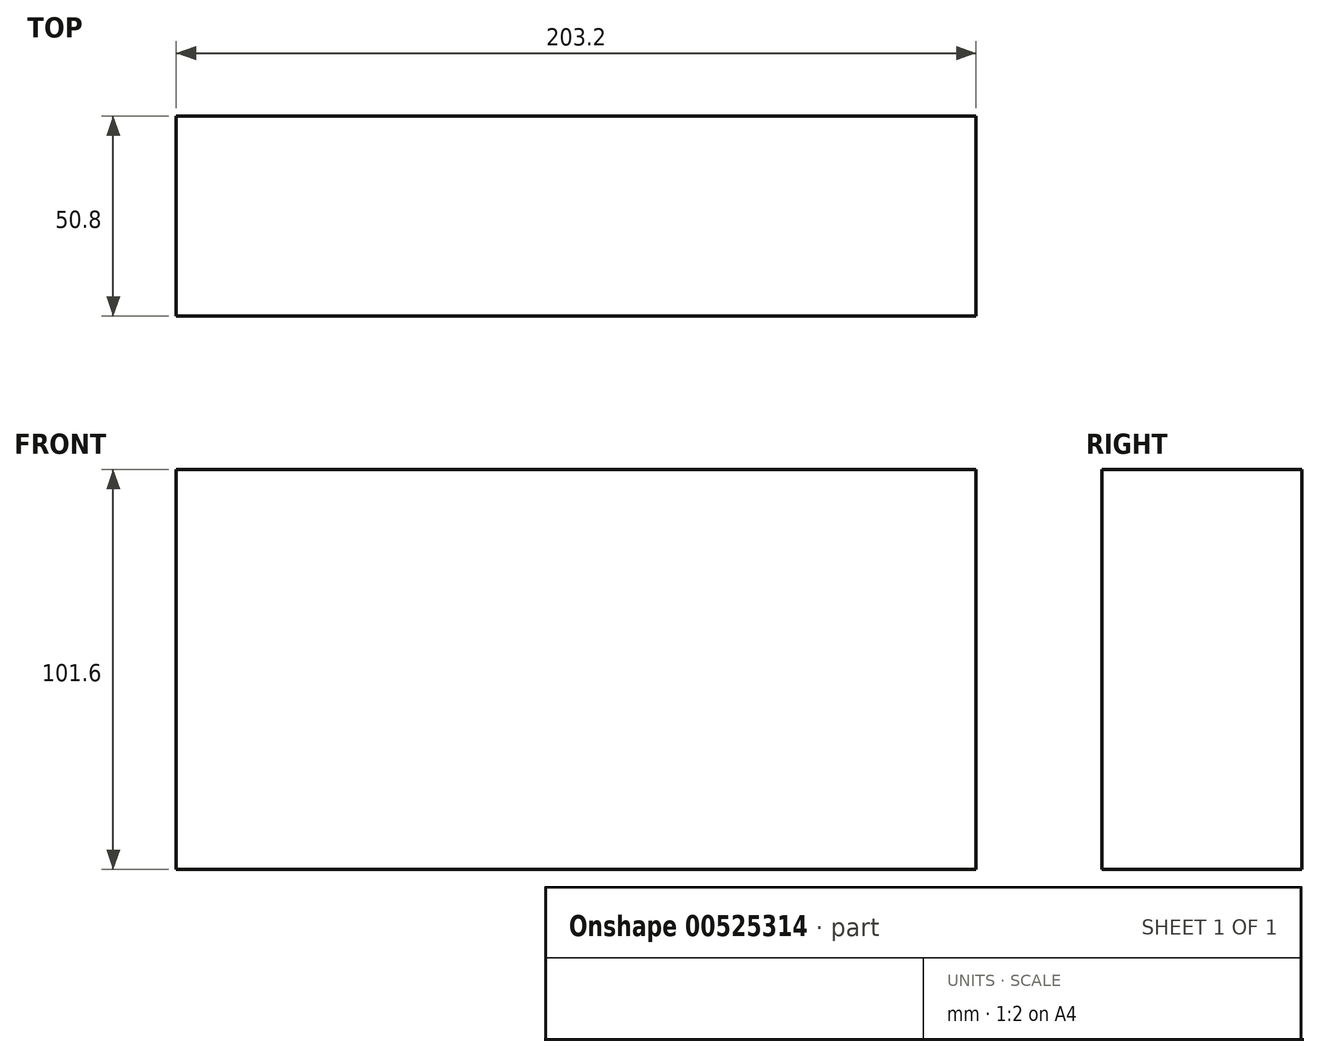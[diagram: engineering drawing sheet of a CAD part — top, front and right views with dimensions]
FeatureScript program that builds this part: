
annotation { "Feature Type Name" : "Feature", "Feature Type Description" : "" }
export const myFeature = defineFeature(function(context is Context, id is Id, definition is map)
    precondition{}
    {
        {
            var Q0;
            Q0=qCreatedBy(makeId("Right.planeOp"),FACE);
            var sketch = newSketch(context, id + "F0", { "sketchPlane" : qUnion([Q0])});
            skLineSegment(sketch, "E0.bottom", {"start": v(0, 0) * mm, "end": v(50.8, 0) * mm});
            skLineSegment(sketch, "E0.top", {"start": v(0, 101.6) * mm, "end": v(50.8, 101.6) * mm});
            skLineSegment(sketch, "E0.left", {"start": v(0, 0) * mm, "end": v(0, 101.6) * mm});
            skLineSegment(sketch, "E0.right", {"start": v(50.8, 0) * mm, "end": v(50.8, 101.6) * mm});
            skSolve(sketch);
        }
        {
            var Q0;
            Q0=makeQuery(id+"F0.imprint","IMPRINT",FACE,{"disambiguationData":[TD([[makeQuery(id+"F0.imprint","IMPRINT",EDGE,{"derivedFrom":sQuery(id+"F0.wireOp",EDGE,"E0.bottom")}),1.0]])]});
            extrude(context, id + "F1", {"entities" : qUnion([Q0]), "depth" : 203.2 * mm, "offsetDistance" : 25.4 * mm});
        }
    });
